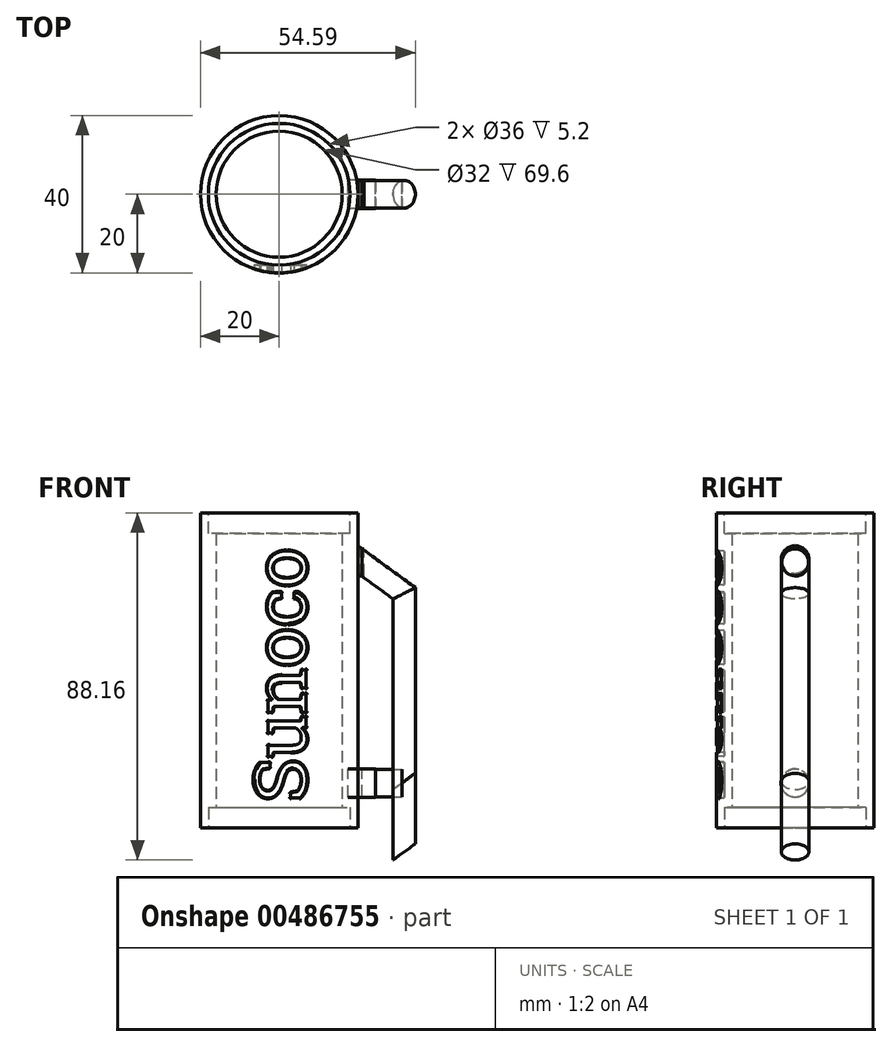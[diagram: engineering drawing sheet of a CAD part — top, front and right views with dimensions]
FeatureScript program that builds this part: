
annotation { "Feature Type Name" : "Feature", "Feature Type Description" : "" }
export const myFeature = defineFeature(function(context is Context, id is Id, definition is map)
    precondition{}
    {
        {
            var Q0;
            Q0=qCreatedBy(makeId("Top.planeOp"),FACE);
            var sketch = newSketch(context, id + "F0", { "sketchPlane" : qUnion([Q0])});
            skCircle(sketch, "E0", {"center": v(0, 0) * mm, "radius": 20 * mm});
            skSolve(sketch);
        }
        {
            var Q0;
            Q0 = qSketchRegion(id + "F0", true);
            extrude(context, id + "F1", {"entities" : qUnion([Q0]), "depth" : 80 * mm, "offsetDistance" : 25 * mm});
        }
        {
            var Q0;
            Q0=makeQuery(id+"F1.opExtrude","CAP_FACE",FACE,{"disambiguationData":[OSD([sQuery(id+"F0.wireOp",EDGE,"E0")])],"isStart":false});
            shell(context, id + "F2", {"entities" : qUnion([Q0]), "thickness" : 4 * mm});
        }
        {
            var Q0;
            Q0=makeQuery(id+"F1.opExtrude","CAP_FACE",FACE,{"disambiguationData":[OSD([sQuery(id+"F0.wireOp",EDGE,"E0")])],"isStart":false});
            var sketch = newSketch(context, id + "F3", { "sketchPlane" : qUnion([Q0])});
            skCircle(sketch, "E1.0", {"center": v(0, 0) * mm, "radius": 16 * mm});
            skCircle(sketch, "E2", {"center": v(0, 0) * mm, "radius": 18 * mm});
            skSolve(sketch);
        }
        {
            var Q0;
            Q0 = qSketchRegion(id + "F3", true);
            extrude(context, id + "F4", {"entities" : qUnion([Q0]), "operationType" : NewBodyOperationType.REMOVE, "oppositeDirection" : true, "depth" : 5.2 * mm, "offsetDistance" : 25 * mm});
        }
        {
            var Q0;
            Q0=makeQuery(id+"F1.opExtrude","CAP_FACE",FACE,{"disambiguationData":[OSD([sQuery(id+"F0.wireOp",EDGE,"E0")])],"isStart":false});
            var sketch = newSketch(context, id + "F5", { "sketchPlane" : qUnion([Q0])});
            skCircle(sketch, "E3.0", {"center": v(0, 0) * mm, "radius": 20 * mm});
            skCircle(sketch, "E4", {"center": v(-18.47, 7.67) * mm, "radius": 1 * mm});
            skSolve(sketch);
        }
        {
            var Q0;
            Q0=qCreatedBy(makeId("Front.planeOp"),FACE);
            cPlane(context, id + "F6", {"entities" : qUnion([Q0]), "cplaneType" : CPlaneType.OFFSET, "offset" : 20 * mm, "width" : 150 * mm, "height" : 150 * mm});
        }
        {
            var Q0;
            Q0=qCreatedBy(id+"F6.planeOp",FACE);
            var sketch = newSketch(context, id + "F7", { "sketchPlane" : qUnion([Q0])});
            skText(sketch, "E5", { "text": "Sunoco", "fontName": "RobotoSlab-Regular.ttf"});
            const initialGuessF7  = {"E5": [0.00686, 0.0065, 0, 1, 0.01323]};
            skSetInitialGuess(sketch, initialGuessF7);
            skSolve(sketch);
        }
        {
            var Q0;
            Q0 = qSketchRegion(id + "F7", true);
            extrude(context, id + "F8", {"entities" : qUnion([Q0]), "operationType" : NewBodyOperationType.REMOVE, "oppositeDirection" : true, "depth" : 1.5 * mm, "offsetDistance" : 25 * mm});
        }
        {
            var Q0;
            Q0 = qSketchRegion(id + "F7", true);
            extrude(context, id + "F9", {"entities" : qUnion([Q0]), "operationType" : NewBodyOperationType.REMOVE, "oppositeDirection" : true, "depth" : 2 * mm, "offsetDistance" : 25 * mm});
        }
        {
            var Q0;
            {var subQ0=sQuery(id+"F7.wireOp",EDGE,"E5.sketch_text.stroke-26");Q0=makeQuery(id+"F9.boolean.opBoolean","MERGE",FACE,{"derivedFrom":[makeQuery(id+"F8.boolean.opBoolean","COPY",FACE,{"derivedFrom":makeQuery(id+"F8.opExtrude","SWEPT_FACE",FACE,{"disambiguationData":[OSD([subQ0])]})}),makeQuery(id+"F9.opExtrude","SWEPT_FACE",FACE,{"disambiguationData":[OSD([subQ0])]})]});}
            var Q1;
            {var subQ0=sQuery(id+"F7.wireOp",EDGE,"E5.sketch_text.stroke-27");Q1=makeQuery(id+"F9.boolean.opBoolean","MERGE",FACE,{"derivedFrom":[makeQuery(id+"F8.boolean.opBoolean","COPY",FACE,{"derivedFrom":makeQuery(id+"F8.opExtrude","SWEPT_FACE",FACE,{"disambiguationData":[OSD([subQ0])]})}),makeQuery(id+"F9.opExtrude","SWEPT_FACE",FACE,{"disambiguationData":[OSD([subQ0])]})]});}
            var Q2;
            {var subQ0=sQuery(id+"F7.wireOp",EDGE,"E5.sketch_text.stroke-24");Q2=makeQuery(id+"F9.boolean.opBoolean","MERGE",FACE,{"derivedFrom":[makeQuery(id+"F8.boolean.opBoolean","COPY",FACE,{"derivedFrom":makeQuery(id+"F8.opExtrude","SWEPT_FACE",FACE,{"disambiguationData":[OSD([subQ0])]})}),makeQuery(id+"F9.opExtrude","SWEPT_FACE",FACE,{"disambiguationData":[OSD([subQ0])]})]});}
            var Q3;
            {var subQ0=sQuery(id+"F7.wireOp",EDGE,"E5.sketch_text.stroke-23");Q3=makeQuery(id+"F9.boolean.opBoolean","MERGE",FACE,{"derivedFrom":[makeQuery(id+"F8.boolean.opBoolean","COPY",FACE,{"derivedFrom":makeQuery(id+"F8.opExtrude","SWEPT_FACE",FACE,{"disambiguationData":[OSD([subQ0])]})}),makeQuery(id+"F9.opExtrude","SWEPT_FACE",FACE,{"disambiguationData":[OSD([subQ0])]})]});}
            var Q4;
            {var subQ0=sQuery(id+"F7.wireOp",EDGE,"E5.sketch_text.stroke-22");Q4=makeQuery(id+"F9.boolean.opBoolean","MERGE",FACE,{"derivedFrom":[makeQuery(id+"F8.boolean.opBoolean","COPY",FACE,{"derivedFrom":makeQuery(id+"F8.opExtrude","SWEPT_FACE",FACE,{"disambiguationData":[OSD([subQ0])]})}),makeQuery(id+"F9.opExtrude","SWEPT_FACE",FACE,{"disambiguationData":[OSD([subQ0])]})]});}
            var Q5;
            {var subQ0=sQuery(id+"F7.wireOp",EDGE,"E5.sketch_text.stroke-21");Q5=makeQuery(id+"F9.boolean.opBoolean","MERGE",FACE,{"derivedFrom":[makeQuery(id+"F8.boolean.opBoolean","COPY",FACE,{"derivedFrom":makeQuery(id+"F8.opExtrude","SWEPT_FACE",FACE,{"disambiguationData":[OSD([subQ0])]})}),makeQuery(id+"F9.opExtrude","SWEPT_FACE",FACE,{"disambiguationData":[OSD([subQ0])]})]});}
            var Q6;
            {var subQ0=sQuery(id+"F7.wireOp",EDGE,"E5.sketch_text.stroke-20");Q6=makeQuery(id+"F9.boolean.opBoolean","MERGE",FACE,{"derivedFrom":[makeQuery(id+"F8.boolean.opBoolean","COPY",FACE,{"derivedFrom":makeQuery(id+"F8.opExtrude","SWEPT_FACE",FACE,{"disambiguationData":[OSD([subQ0])]})}),makeQuery(id+"F9.opExtrude","SWEPT_FACE",FACE,{"disambiguationData":[OSD([subQ0])]})]});}
            var Q7;
            {var subQ0=sQuery(id+"F7.wireOp",EDGE,"E5.sketch_text.stroke-19");Q7=makeQuery(id+"F9.boolean.opBoolean","MERGE",FACE,{"derivedFrom":[makeQuery(id+"F8.boolean.opBoolean","COPY",FACE,{"derivedFrom":makeQuery(id+"F8.opExtrude","SWEPT_FACE",FACE,{"disambiguationData":[OSD([subQ0])]})}),makeQuery(id+"F9.opExtrude","SWEPT_FACE",FACE,{"disambiguationData":[OSD([subQ0])]})]});}
            var Q8;
            {var subQ0=sQuery(id+"F7.wireOp",EDGE,"E5.sketch_text.stroke-18");Q8=makeQuery(id+"F9.boolean.opBoolean","MERGE",FACE,{"derivedFrom":[makeQuery(id+"F8.boolean.opBoolean","COPY",FACE,{"derivedFrom":makeQuery(id+"F8.opExtrude","SWEPT_FACE",FACE,{"disambiguationData":[OSD([subQ0])]})}),makeQuery(id+"F9.opExtrude","SWEPT_FACE",FACE,{"disambiguationData":[OSD([subQ0])]})]});}
            var Q9;
            {var subQ0=sQuery(id+"F7.wireOp",EDGE,"E5.sketch_text.stroke-17");Q9=makeQuery(id+"F9.boolean.opBoolean","MERGE",FACE,{"derivedFrom":[makeQuery(id+"F8.boolean.opBoolean","COPY",FACE,{"derivedFrom":makeQuery(id+"F8.opExtrude","SWEPT_FACE",FACE,{"disambiguationData":[OSD([subQ0])]})}),makeQuery(id+"F9.opExtrude","SWEPT_FACE",FACE,{"disambiguationData":[OSD([subQ0])]})]});}
            var Q10;
            {var subQ0=sQuery(id+"F7.wireOp",EDGE,"E5.sketch_text.stroke-16");Q10=makeQuery(id+"F9.boolean.opBoolean","MERGE",FACE,{"derivedFrom":[makeQuery(id+"F8.boolean.opBoolean","COPY",FACE,{"derivedFrom":makeQuery(id+"F8.opExtrude","SWEPT_FACE",FACE,{"disambiguationData":[OSD([subQ0])]})}),makeQuery(id+"F9.opExtrude","SWEPT_FACE",FACE,{"disambiguationData":[OSD([subQ0])]})]});}
            var Q11;
            {var subQ0=sQuery(id+"F7.wireOp",EDGE,"E5.sketch_text.stroke-15");Q11=makeQuery(id+"F9.boolean.opBoolean","MERGE",FACE,{"derivedFrom":[makeQuery(id+"F8.boolean.opBoolean","COPY",FACE,{"derivedFrom":makeQuery(id+"F8.opExtrude","SWEPT_FACE",FACE,{"disambiguationData":[OSD([subQ0])]})}),makeQuery(id+"F9.opExtrude","SWEPT_FACE",FACE,{"disambiguationData":[OSD([subQ0])]})]});}
            var Q12;
            {var subQ0=sQuery(id+"F7.wireOp",EDGE,"E5.sketch_text.stroke-14");Q12=makeQuery(id+"F9.boolean.opBoolean","MERGE",FACE,{"derivedFrom":[makeQuery(id+"F8.boolean.opBoolean","COPY",FACE,{"derivedFrom":makeQuery(id+"F8.opExtrude","SWEPT_FACE",FACE,{"disambiguationData":[OSD([subQ0])]})}),makeQuery(id+"F9.opExtrude","SWEPT_FACE",FACE,{"disambiguationData":[OSD([subQ0])]})]});}
            var Q13;
            {var subQ0=sQuery(id+"F7.wireOp",EDGE,"E5.sketch_text.stroke-13");Q13=makeQuery(id+"F9.boolean.opBoolean","MERGE",FACE,{"derivedFrom":[makeQuery(id+"F8.boolean.opBoolean","COPY",FACE,{"derivedFrom":makeQuery(id+"F8.opExtrude","SWEPT_FACE",FACE,{"disambiguationData":[OSD([subQ0])]})}),makeQuery(id+"F9.opExtrude","SWEPT_FACE",FACE,{"disambiguationData":[OSD([subQ0])]})]});}
            var Q14;
            {var subQ0=sQuery(id+"F7.wireOp",EDGE,"E5.sketch_text.stroke-12");Q14=makeQuery(id+"F9.boolean.opBoolean","MERGE",FACE,{"derivedFrom":[makeQuery(id+"F8.boolean.opBoolean","COPY",FACE,{"derivedFrom":makeQuery(id+"F8.opExtrude","SWEPT_FACE",FACE,{"disambiguationData":[OSD([subQ0])]})}),makeQuery(id+"F9.opExtrude","SWEPT_FACE",FACE,{"disambiguationData":[OSD([subQ0])]})]});}
            var Q15;
            {var subQ0=sQuery(id+"F7.wireOp",EDGE,"E5.sketch_text.stroke-11");Q15=makeQuery(id+"F9.boolean.opBoolean","MERGE",FACE,{"derivedFrom":[makeQuery(id+"F8.boolean.opBoolean","COPY",FACE,{"derivedFrom":makeQuery(id+"F8.opExtrude","SWEPT_FACE",FACE,{"disambiguationData":[OSD([subQ0])]})}),makeQuery(id+"F9.opExtrude","SWEPT_FACE",FACE,{"disambiguationData":[OSD([subQ0])]})]});}
            var Q16;
            {var subQ0=sQuery(id+"F7.wireOp",EDGE,"E5.sketch_text.stroke-10");Q16=makeQuery(id+"F9.boolean.opBoolean","MERGE",FACE,{"derivedFrom":[makeQuery(id+"F8.boolean.opBoolean","COPY",FACE,{"derivedFrom":makeQuery(id+"F8.opExtrude","SWEPT_FACE",FACE,{"disambiguationData":[OSD([subQ0])]})}),makeQuery(id+"F9.opExtrude","SWEPT_FACE",FACE,{"disambiguationData":[OSD([subQ0])]})]});}
            var Q17;
            {var subQ0=sQuery(id+"F7.wireOp",EDGE,"E5.sketch_text.stroke-9");Q17=makeQuery(id+"F9.boolean.opBoolean","MERGE",FACE,{"derivedFrom":[makeQuery(id+"F8.boolean.opBoolean","COPY",FACE,{"derivedFrom":makeQuery(id+"F8.opExtrude","SWEPT_FACE",FACE,{"disambiguationData":[OSD([subQ0])]})}),makeQuery(id+"F9.opExtrude","SWEPT_FACE",FACE,{"disambiguationData":[OSD([subQ0])]})]});}
            var Q18;
            {var subQ0=sQuery(id+"F7.wireOp",EDGE,"E5.sketch_text.stroke-8");Q18=makeQuery(id+"F9.boolean.opBoolean","MERGE",FACE,{"derivedFrom":[makeQuery(id+"F8.boolean.opBoolean","COPY",FACE,{"derivedFrom":makeQuery(id+"F8.opExtrude","SWEPT_FACE",FACE,{"disambiguationData":[OSD([subQ0])]})}),makeQuery(id+"F9.opExtrude","SWEPT_FACE",FACE,{"disambiguationData":[OSD([subQ0])]})]});}
            var Q19;
            {var subQ0=sQuery(id+"F7.wireOp",EDGE,"E5.sketch_text.stroke-7");Q19=makeQuery(id+"F9.boolean.opBoolean","MERGE",FACE,{"derivedFrom":[makeQuery(id+"F8.boolean.opBoolean","COPY",FACE,{"derivedFrom":makeQuery(id+"F8.opExtrude","SWEPT_FACE",FACE,{"disambiguationData":[OSD([subQ0])]})}),makeQuery(id+"F9.opExtrude","SWEPT_FACE",FACE,{"disambiguationData":[OSD([subQ0])]})]});}
            var Q20;
            {var subQ0=sQuery(id+"F7.wireOp",EDGE,"E5.sketch_text.stroke-6");Q20=makeQuery(id+"F9.boolean.opBoolean","MERGE",FACE,{"derivedFrom":[makeQuery(id+"F8.boolean.opBoolean","COPY",FACE,{"derivedFrom":makeQuery(id+"F8.opExtrude","SWEPT_FACE",FACE,{"disambiguationData":[OSD([subQ0])]})}),makeQuery(id+"F9.opExtrude","SWEPT_FACE",FACE,{"disambiguationData":[OSD([subQ0])]})]});}
            var Q21;
            {var subQ0=sQuery(id+"F7.wireOp",EDGE,"E5.sketch_text.stroke-5");Q21=makeQuery(id+"F9.boolean.opBoolean","MERGE",FACE,{"derivedFrom":[makeQuery(id+"F8.boolean.opBoolean","COPY",FACE,{"derivedFrom":makeQuery(id+"F8.opExtrude","SWEPT_FACE",FACE,{"disambiguationData":[OSD([subQ0])]})}),makeQuery(id+"F9.opExtrude","SWEPT_FACE",FACE,{"disambiguationData":[OSD([subQ0])]})]});}
            var Q22;
            {var subQ0=sQuery(id+"F7.wireOp",EDGE,"E5.sketch_text.stroke-4");Q22=makeQuery(id+"F9.boolean.opBoolean","MERGE",FACE,{"derivedFrom":[makeQuery(id+"F8.boolean.opBoolean","COPY",FACE,{"derivedFrom":makeQuery(id+"F8.opExtrude","SWEPT_FACE",FACE,{"disambiguationData":[OSD([subQ0])]})}),makeQuery(id+"F9.opExtrude","SWEPT_FACE",FACE,{"disambiguationData":[OSD([subQ0])]})]});}
            var Q23;
            {var subQ0=sQuery(id+"F7.wireOp",EDGE,"E5.sketch_text.stroke-3");Q23=makeQuery(id+"F9.boolean.opBoolean","MERGE",FACE,{"derivedFrom":[makeQuery(id+"F8.boolean.opBoolean","COPY",FACE,{"derivedFrom":makeQuery(id+"F8.opExtrude","SWEPT_FACE",FACE,{"disambiguationData":[OSD([subQ0])]})}),makeQuery(id+"F9.opExtrude","SWEPT_FACE",FACE,{"disambiguationData":[OSD([subQ0])]})]});}
            var Q24;
            Q24=makeQuery(id+"F8.boolean.opBoolean","INTERSECT",EDGE,{"derivedFrom":[makeQuery(id+"F1.opExtrude","SWEPT_FACE",FACE,{"disambiguationData":[OSD([sQuery(id+"F0.wireOp",EDGE,"E0")])]}),makeQuery(id+"F8.opExtrude","SWEPT_FACE",FACE,{"disambiguationData":[OSD([sQuery(id+"F7.wireOp",EDGE,"E5.sketch_text.stroke-2")])]})]});
            var Q25;
            Q25=makeQuery(id+"F9.boolean.opBoolean","COPY",EDGE,{"derivedFrom":makeQuery(id+"F9.opExtrude","CAP_EDGE",EDGE,{"disambiguationData":[OSD([sQuery(id+"F7.wireOp",EDGE,"E5.sketch_text.stroke-2")])],"isStart":false})});
            var Q26;
            {var subQ0=sQuery(id+"F7.wireOp",EDGE,"E5.sketch_text.stroke-2");Q26=makeQuery(id+"F9.boolean.opBoolean","MERGE",FACE,{"derivedFrom":[makeQuery(id+"F8.boolean.opBoolean","COPY",FACE,{"derivedFrom":makeQuery(id+"F8.opExtrude","SWEPT_FACE",FACE,{"disambiguationData":[OSD([subQ0])]})}),makeQuery(id+"F9.opExtrude","SWEPT_FACE",FACE,{"disambiguationData":[OSD([subQ0])]})]});}
            var Q27;
            {var subQ0=sQuery(id+"F7.wireOp",EDGE,"E5.sketch_text.stroke-1");Q27=makeQuery(id+"F9.boolean.opBoolean","MERGE",FACE,{"derivedFrom":[makeQuery(id+"F8.boolean.opBoolean","COPY",FACE,{"derivedFrom":makeQuery(id+"F8.opExtrude","SWEPT_FACE",FACE,{"disambiguationData":[OSD([subQ0])]})}),makeQuery(id+"F9.opExtrude","SWEPT_FACE",FACE,{"disambiguationData":[OSD([subQ0])]})]});}
            var Q28;
            {var subQ0=sQuery(id+"F7.wireOp",EDGE,"E5.sketch_text.stroke-0");Q28=makeQuery(id+"F9.boolean.opBoolean","MERGE",FACE,{"derivedFrom":[makeQuery(id+"F8.boolean.opBoolean","COPY",FACE,{"derivedFrom":makeQuery(id+"F8.opExtrude","SWEPT_FACE",FACE,{"disambiguationData":[OSD([subQ0])]})}),makeQuery(id+"F9.opExtrude","SWEPT_FACE",FACE,{"disambiguationData":[OSD([subQ0])]})]});}
            fillet(context, id + "F10", {"entities" : qUnion([Q0, Q1, Q2, Q3, Q4, Q5, Q6, Q7, Q8, Q9, Q10, Q11, Q12, Q13, Q14, Q15, Q16, Q17, Q18, Q19, Q20, Q21, Q22, Q23, Q24, Q25, Q26, Q27, Q28]), "radius" : .2 * mm, "tangentPropagation" : true, "allowEdgeOverflow" : false});
        }
        {
            var Q0;
            {var subQ0=sQuery(id+"F7.wireOp",EDGE,"E5.sketch_text.stroke-38");var subQ1=sQuery(id+"F7.wireOp",EDGE,"E5.sketch_text.stroke-37");Q0=makeQuery(id+"F9.boolean.opBoolean","MERGE",FACE,{"derivedFrom":[makeQuery(id+"F8.boolean.opBoolean","COPY",FACE,{"derivedFrom":makeQuery(id+"F8.opExtrude","SWEPT_FACE",FACE,{"disambiguationData":[OSD([subQ1,subQ0])]})}),makeQuery(id+"F9.opExtrude","SWEPT_FACE",FACE,{"disambiguationData":[OSD([subQ1,subQ0])]})]});}
            var Q1;
            {var subQ0=sQuery(id+"F7.wireOp",EDGE,"E5.sketch_text.stroke-36");Q1=makeQuery(id+"F9.boolean.opBoolean","MERGE",FACE,{"derivedFrom":[makeQuery(id+"F8.boolean.opBoolean","COPY",FACE,{"derivedFrom":makeQuery(id+"F8.opExtrude","SWEPT_FACE",FACE,{"disambiguationData":[OSD([subQ0])]})}),makeQuery(id+"F9.opExtrude","SWEPT_FACE",FACE,{"disambiguationData":[OSD([subQ0])]})]});}
            var Q2;
            {var subQ0=sQuery(id+"F7.wireOp",EDGE,"E5.sketch_text.stroke-35");Q2=makeQuery(id+"F9.boolean.opBoolean","MERGE",FACE,{"derivedFrom":[makeQuery(id+"F8.boolean.opBoolean","COPY",FACE,{"derivedFrom":makeQuery(id+"F8.opExtrude","SWEPT_FACE",FACE,{"disambiguationData":[OSD([subQ0])]})}),makeQuery(id+"F9.opExtrude","SWEPT_FACE",FACE,{"disambiguationData":[OSD([subQ0])]})]});}
            var Q3;
            {var subQ0=sQuery(id+"F7.wireOp",EDGE,"E5.sketch_text.stroke-34");Q3=makeQuery(id+"F9.boolean.opBoolean","MERGE",FACE,{"derivedFrom":[makeQuery(id+"F8.boolean.opBoolean","COPY",FACE,{"derivedFrom":makeQuery(id+"F8.opExtrude","SWEPT_FACE",FACE,{"disambiguationData":[OSD([subQ0])]})}),makeQuery(id+"F9.opExtrude","SWEPT_FACE",FACE,{"disambiguationData":[OSD([subQ0])]})]});}
            var Q4;
            {var subQ0=sQuery(id+"F7.wireOp",EDGE,"E5.sketch_text.stroke-44");Q4=makeQuery(id+"F9.boolean.opBoolean","MERGE",FACE,{"derivedFrom":[makeQuery(id+"F8.boolean.opBoolean","COPY",FACE,{"derivedFrom":makeQuery(id+"F8.opExtrude","SWEPT_FACE",FACE,{"disambiguationData":[OSD([subQ0])]})}),makeQuery(id+"F9.opExtrude","SWEPT_FACE",FACE,{"disambiguationData":[OSD([subQ0])]})]});}
            var Q5;
            {var subQ0=sQuery(id+"F7.wireOp",EDGE,"E5.sketch_text.stroke-45");Q5=makeQuery(id+"F9.boolean.opBoolean","MERGE",FACE,{"derivedFrom":[makeQuery(id+"F8.boolean.opBoolean","COPY",FACE,{"derivedFrom":makeQuery(id+"F8.opExtrude","SWEPT_FACE",FACE,{"disambiguationData":[OSD([subQ0])]})}),makeQuery(id+"F9.opExtrude","SWEPT_FACE",FACE,{"disambiguationData":[OSD([subQ0])]})]});}
            var Q6;
            {var subQ0=sQuery(id+"F7.wireOp",EDGE,"E5.sketch_text.stroke-46");Q6=makeQuery(id+"F9.boolean.opBoolean","MERGE",FACE,{"derivedFrom":[makeQuery(id+"F8.boolean.opBoolean","COPY",FACE,{"derivedFrom":makeQuery(id+"F8.opExtrude","SWEPT_FACE",FACE,{"disambiguationData":[OSD([subQ0])]})}),makeQuery(id+"F9.opExtrude","SWEPT_FACE",FACE,{"disambiguationData":[OSD([subQ0])]})]});}
            var Q7;
            {var subQ0=sQuery(id+"F7.wireOp",EDGE,"E5.sketch_text.stroke-48");var subQ1=sQuery(id+"F7.wireOp",EDGE,"E5.sketch_text.stroke-47");Q7=makeQuery(id+"F9.boolean.opBoolean","MERGE",FACE,{"derivedFrom":[makeQuery(id+"F8.boolean.opBoolean","COPY",FACE,{"derivedFrom":makeQuery(id+"F8.opExtrude","SWEPT_FACE",FACE,{"disambiguationData":[OSD([subQ1,subQ0])]})}),makeQuery(id+"F9.opExtrude","SWEPT_FACE",FACE,{"disambiguationData":[OSD([subQ1,subQ0])]})]});}
            var Q8;
            {var subQ0=sQuery(id+"F7.wireOp",EDGE,"E5.sketch_text.stroke-49");Q8=makeQuery(id+"F9.boolean.opBoolean","MERGE",FACE,{"derivedFrom":[makeQuery(id+"F8.boolean.opBoolean","COPY",FACE,{"derivedFrom":makeQuery(id+"F8.opExtrude","SWEPT_FACE",FACE,{"disambiguationData":[OSD([subQ0])]})}),makeQuery(id+"F9.opExtrude","SWEPT_FACE",FACE,{"disambiguationData":[OSD([subQ0])]})]});}
            var Q9;
            {var subQ0=sQuery(id+"F7.wireOp",EDGE,"E5.sketch_text.stroke-52");Q9=makeQuery(id+"F9.boolean.opBoolean","MERGE",FACE,{"derivedFrom":[makeQuery(id+"F8.boolean.opBoolean","COPY",FACE,{"derivedFrom":makeQuery(id+"F8.opExtrude","SWEPT_FACE",FACE,{"disambiguationData":[OSD([subQ0])]})}),makeQuery(id+"F9.opExtrude","SWEPT_FACE",FACE,{"disambiguationData":[OSD([subQ0])]})]});}
            var Q10;
            {var subQ0=sQuery(id+"F7.wireOp",EDGE,"E5.sketch_text.stroke-53");Q10=makeQuery(id+"F9.boolean.opBoolean","MERGE",FACE,{"derivedFrom":[makeQuery(id+"F8.boolean.opBoolean","COPY",FACE,{"derivedFrom":makeQuery(id+"F8.opExtrude","SWEPT_FACE",FACE,{"disambiguationData":[OSD([subQ0])]})}),makeQuery(id+"F9.opExtrude","SWEPT_FACE",FACE,{"disambiguationData":[OSD([subQ0])]})]});}
            var Q11;
            {var subQ0=sQuery(id+"F7.wireOp",EDGE,"E5.sketch_text.stroke-50");Q11=makeQuery(id+"F9.boolean.opBoolean","MERGE",FACE,{"derivedFrom":[makeQuery(id+"F8.boolean.opBoolean","COPY",FACE,{"derivedFrom":makeQuery(id+"F8.opExtrude","SWEPT_FACE",FACE,{"disambiguationData":[OSD([subQ0])]})}),makeQuery(id+"F9.opExtrude","SWEPT_FACE",FACE,{"disambiguationData":[OSD([subQ0])]})]});}
            var Q12;
            {var subQ0=sQuery(id+"F7.wireOp",EDGE,"E5.sketch_text.stroke-78");Q12=makeQuery(id+"F9.boolean.opBoolean","MERGE",FACE,{"derivedFrom":[makeQuery(id+"F8.boolean.opBoolean","COPY",FACE,{"derivedFrom":makeQuery(id+"F8.opExtrude","SWEPT_FACE",FACE,{"disambiguationData":[OSD([subQ0])]})}),makeQuery(id+"F9.opExtrude","SWEPT_FACE",FACE,{"disambiguationData":[OSD([subQ0])]})]});}
            var Q13;
            {var subQ0=sQuery(id+"F7.wireOp",EDGE,"E5.sketch_text.stroke-79");Q13=makeQuery(id+"F9.boolean.opBoolean","MERGE",FACE,{"derivedFrom":[makeQuery(id+"F8.boolean.opBoolean","COPY",FACE,{"derivedFrom":makeQuery(id+"F8.opExtrude","SWEPT_FACE",FACE,{"disambiguationData":[OSD([subQ0])]})}),makeQuery(id+"F9.opExtrude","SWEPT_FACE",FACE,{"disambiguationData":[OSD([subQ0])]})]});}
            var Q14;
            {var subQ0=sQuery(id+"F7.wireOp",EDGE,"E5.sketch_text.stroke-54");Q14=makeQuery(id+"F9.boolean.opBoolean","MERGE",FACE,{"derivedFrom":[makeQuery(id+"F8.boolean.opBoolean","COPY",FACE,{"derivedFrom":makeQuery(id+"F8.opExtrude","SWEPT_FACE",FACE,{"disambiguationData":[OSD([subQ0])]})}),makeQuery(id+"F9.opExtrude","SWEPT_FACE",FACE,{"disambiguationData":[OSD([subQ0])]})]});}
            var Q15;
            {var subQ0=sQuery(id+"F7.wireOp",EDGE,"E5.sketch_text.stroke-55");Q15=makeQuery(id+"F9.boolean.opBoolean","MERGE",FACE,{"derivedFrom":[makeQuery(id+"F8.boolean.opBoolean","COPY",FACE,{"derivedFrom":makeQuery(id+"F8.opExtrude","SWEPT_FACE",FACE,{"disambiguationData":[OSD([subQ0])]})}),makeQuery(id+"F9.opExtrude","SWEPT_FACE",FACE,{"disambiguationData":[OSD([subQ0])]})]});}
            var Q16;
            {var subQ0=sQuery(id+"F7.wireOp",EDGE,"E5.sketch_text.stroke-56");Q16=makeQuery(id+"F9.boolean.opBoolean","MERGE",FACE,{"derivedFrom":[makeQuery(id+"F8.boolean.opBoolean","COPY",FACE,{"derivedFrom":makeQuery(id+"F8.opExtrude","SWEPT_FACE",FACE,{"disambiguationData":[OSD([subQ0])]})}),makeQuery(id+"F9.opExtrude","SWEPT_FACE",FACE,{"disambiguationData":[OSD([subQ0])]})]});}
            var Q17;
            {var subQ0=sQuery(id+"F7.wireOp",EDGE,"E5.sketch_text.stroke-57");Q17=makeQuery(id+"F9.boolean.opBoolean","MERGE",FACE,{"derivedFrom":[makeQuery(id+"F8.boolean.opBoolean","COPY",FACE,{"derivedFrom":makeQuery(id+"F8.opExtrude","SWEPT_FACE",FACE,{"disambiguationData":[OSD([subQ0])]})}),makeQuery(id+"F9.opExtrude","SWEPT_FACE",FACE,{"disambiguationData":[OSD([subQ0])]})]});}
            var Q18;
            {var subQ0=sQuery(id+"F7.wireOp",EDGE,"E5.sketch_text.stroke-58");Q18=makeQuery(id+"F9.boolean.opBoolean","MERGE",FACE,{"derivedFrom":[makeQuery(id+"F8.boolean.opBoolean","COPY",FACE,{"derivedFrom":makeQuery(id+"F8.opExtrude","SWEPT_FACE",FACE,{"disambiguationData":[OSD([subQ0])]})}),makeQuery(id+"F9.opExtrude","SWEPT_FACE",FACE,{"disambiguationData":[OSD([subQ0])]})]});}
            var Q19;
            {var subQ0=sQuery(id+"F7.wireOp",EDGE,"E5.sketch_text.stroke-59");Q19=makeQuery(id+"F9.boolean.opBoolean","MERGE",FACE,{"derivedFrom":[makeQuery(id+"F8.boolean.opBoolean","COPY",FACE,{"derivedFrom":makeQuery(id+"F8.opExtrude","SWEPT_FACE",FACE,{"disambiguationData":[OSD([subQ0])]})}),makeQuery(id+"F9.opExtrude","SWEPT_FACE",FACE,{"disambiguationData":[OSD([subQ0])]})]});}
            var Q20;
            {var subQ0=sQuery(id+"F7.wireOp",EDGE,"E5.sketch_text.stroke-75");Q20=makeQuery(id+"F9.boolean.opBoolean","MERGE",FACE,{"derivedFrom":[makeQuery(id+"F8.boolean.opBoolean","COPY",FACE,{"derivedFrom":makeQuery(id+"F8.opExtrude","SWEPT_FACE",FACE,{"disambiguationData":[OSD([subQ0])]})}),makeQuery(id+"F9.opExtrude","SWEPT_FACE",FACE,{"disambiguationData":[OSD([subQ0])]})]});}
            var Q21;
            {var subQ0=sQuery(id+"F7.wireOp",EDGE,"E5.sketch_text.stroke-76");Q21=makeQuery(id+"F9.boolean.opBoolean","MERGE",FACE,{"derivedFrom":[makeQuery(id+"F8.boolean.opBoolean","COPY",FACE,{"derivedFrom":makeQuery(id+"F8.opExtrude","SWEPT_FACE",FACE,{"disambiguationData":[OSD([subQ0])]})}),makeQuery(id+"F9.opExtrude","SWEPT_FACE",FACE,{"disambiguationData":[OSD([subQ0])]})]});}
            var Q22;
            {var subQ0=sQuery(id+"F7.wireOp",EDGE,"E5.sketch_text.stroke-74");Q22=makeQuery(id+"F9.boolean.opBoolean","MERGE",FACE,{"derivedFrom":[makeQuery(id+"F8.boolean.opBoolean","COPY",FACE,{"derivedFrom":makeQuery(id+"F8.opExtrude","SWEPT_FACE",FACE,{"disambiguationData":[OSD([subQ0])]})}),makeQuery(id+"F9.opExtrude","SWEPT_FACE",FACE,{"disambiguationData":[OSD([subQ0])]})]});}
            var Q23;
            {var subQ0=sQuery(id+"F7.wireOp",EDGE,"E5.sketch_text.stroke-73");Q23=makeQuery(id+"F9.boolean.opBoolean","MERGE",FACE,{"derivedFrom":[makeQuery(id+"F8.boolean.opBoolean","COPY",FACE,{"derivedFrom":makeQuery(id+"F8.opExtrude","SWEPT_FACE",FACE,{"disambiguationData":[OSD([subQ0])]})}),makeQuery(id+"F9.opExtrude","SWEPT_FACE",FACE,{"disambiguationData":[OSD([subQ0])]})]});}
            var Q24;
            Q24=makeQuery(id+"F8.boolean.opBoolean","INTERSECT",EDGE,{"derivedFrom":[makeQuery(id+"F1.opExtrude","SWEPT_FACE",FACE,{"disambiguationData":[OSD([sQuery(id+"F0.wireOp",EDGE,"E0")])]}),makeQuery(id+"F8.opExtrude","SWEPT_FACE",FACE,{"disambiguationData":[OSD([sQuery(id+"F7.wireOp",EDGE,"E5.sketch_text.stroke-72")])]})]});
            var Q25;
            {var subQ0=sQuery(id+"F7.wireOp",EDGE,"E5.sketch_text.stroke-72");Q25=makeQuery(id+"F9.boolean.opBoolean","MERGE",FACE,{"derivedFrom":[makeQuery(id+"F8.boolean.opBoolean","COPY",FACE,{"derivedFrom":makeQuery(id+"F8.opExtrude","SWEPT_FACE",FACE,{"disambiguationData":[OSD([subQ0])]})}),makeQuery(id+"F9.opExtrude","SWEPT_FACE",FACE,{"disambiguationData":[OSD([subQ0])]})]});}
            var Q26;
            {var subQ0=sQuery(id+"F7.wireOp",EDGE,"E5.sketch_text.stroke-71");Q26=makeQuery(id+"F9.boolean.opBoolean","MERGE",FACE,{"derivedFrom":[makeQuery(id+"F8.boolean.opBoolean","COPY",FACE,{"derivedFrom":makeQuery(id+"F8.opExtrude","SWEPT_FACE",FACE,{"disambiguationData":[OSD([subQ0])]})}),makeQuery(id+"F9.opExtrude","SWEPT_FACE",FACE,{"disambiguationData":[OSD([subQ0])]})]});}
            var Q27;
            {var subQ0=sQuery(id+"F7.wireOp",EDGE,"E5.sketch_text.stroke-70");Q27=makeQuery(id+"F9.boolean.opBoolean","MERGE",FACE,{"derivedFrom":[makeQuery(id+"F8.boolean.opBoolean","COPY",FACE,{"derivedFrom":makeQuery(id+"F8.opExtrude","SWEPT_FACE",FACE,{"disambiguationData":[OSD([subQ0])]})}),makeQuery(id+"F9.opExtrude","SWEPT_FACE",FACE,{"disambiguationData":[OSD([subQ0])]})]});}
            var Q28;
            {var subQ0=sQuery(id+"F7.wireOp",EDGE,"E5.sketch_text.stroke-69");Q28=makeQuery(id+"F9.boolean.opBoolean","MERGE",FACE,{"derivedFrom":[makeQuery(id+"F8.boolean.opBoolean","COPY",FACE,{"derivedFrom":makeQuery(id+"F8.opExtrude","SWEPT_FACE",FACE,{"disambiguationData":[OSD([subQ0])]})}),makeQuery(id+"F9.opExtrude","SWEPT_FACE",FACE,{"disambiguationData":[OSD([subQ0])]})]});}
            var Q29;
            {var subQ0=sQuery(id+"F7.wireOp",EDGE,"E5.sketch_text.stroke-68");Q29=makeQuery(id+"F9.boolean.opBoolean","MERGE",FACE,{"derivedFrom":[makeQuery(id+"F8.boolean.opBoolean","COPY",FACE,{"derivedFrom":makeQuery(id+"F8.opExtrude","SWEPT_FACE",FACE,{"disambiguationData":[OSD([subQ0])]})}),makeQuery(id+"F9.opExtrude","SWEPT_FACE",FACE,{"disambiguationData":[OSD([subQ0])]})]});}
            var Q30;
            {var subQ0=sQuery(id+"F7.wireOp",EDGE,"E5.sketch_text.stroke-67");Q30=makeQuery(id+"F9.boolean.opBoolean","MERGE",FACE,{"derivedFrom":[makeQuery(id+"F8.boolean.opBoolean","COPY",FACE,{"derivedFrom":makeQuery(id+"F8.opExtrude","SWEPT_FACE",FACE,{"disambiguationData":[OSD([subQ0])]})}),makeQuery(id+"F9.opExtrude","SWEPT_FACE",FACE,{"disambiguationData":[OSD([subQ0])]})]});}
            var Q31;
            {var subQ0=sQuery(id+"F7.wireOp",EDGE,"E5.sketch_text.stroke-66");Q31=makeQuery(id+"F9.boolean.opBoolean","MERGE",FACE,{"derivedFrom":[makeQuery(id+"F8.boolean.opBoolean","COPY",FACE,{"derivedFrom":makeQuery(id+"F8.opExtrude","SWEPT_FACE",FACE,{"disambiguationData":[OSD([subQ0])]})}),makeQuery(id+"F9.opExtrude","SWEPT_FACE",FACE,{"disambiguationData":[OSD([subQ0])]})]});}
            var Q32;
            {var subQ0=sQuery(id+"F7.wireOp",EDGE,"E5.sketch_text.stroke-65");Q32=makeQuery(id+"F9.boolean.opBoolean","MERGE",FACE,{"derivedFrom":[makeQuery(id+"F8.boolean.opBoolean","COPY",FACE,{"derivedFrom":makeQuery(id+"F8.opExtrude","SWEPT_FACE",FACE,{"disambiguationData":[OSD([subQ0])]})}),makeQuery(id+"F9.opExtrude","SWEPT_FACE",FACE,{"disambiguationData":[OSD([subQ0])]})]});}
            var Q33;
            {var subQ0=sQuery(id+"F7.wireOp",EDGE,"E5.sketch_text.stroke-64");Q33=makeQuery(id+"F9.boolean.opBoolean","MERGE",FACE,{"derivedFrom":[makeQuery(id+"F8.boolean.opBoolean","COPY",FACE,{"derivedFrom":makeQuery(id+"F8.opExtrude","SWEPT_FACE",FACE,{"disambiguationData":[OSD([subQ0])]})}),makeQuery(id+"F9.opExtrude","SWEPT_FACE",FACE,{"disambiguationData":[OSD([subQ0])]})]});}
            var Q34;
            {var subQ0=sQuery(id+"F7.wireOp",EDGE,"E5.sketch_text.stroke-63");Q34=makeQuery(id+"F9.boolean.opBoolean","MERGE",FACE,{"derivedFrom":[makeQuery(id+"F8.boolean.opBoolean","COPY",FACE,{"derivedFrom":makeQuery(id+"F8.opExtrude","SWEPT_FACE",FACE,{"disambiguationData":[OSD([subQ0])]})}),makeQuery(id+"F9.opExtrude","SWEPT_FACE",FACE,{"disambiguationData":[OSD([subQ0])]})]});}
            var Q35;
            {var subQ0=sQuery(id+"F7.wireOp",EDGE,"E5.sketch_text.stroke-62");Q35=makeQuery(id+"F9.boolean.opBoolean","MERGE",FACE,{"derivedFrom":[makeQuery(id+"F8.boolean.opBoolean","COPY",FACE,{"derivedFrom":makeQuery(id+"F8.opExtrude","SWEPT_FACE",FACE,{"disambiguationData":[OSD([subQ0])]})}),makeQuery(id+"F9.opExtrude","SWEPT_FACE",FACE,{"disambiguationData":[OSD([subQ0])]})]});}
            var Q36;
            {var subQ0=sQuery(id+"F7.wireOp",EDGE,"E5.sketch_text.stroke-61");Q36=makeQuery(id+"F9.boolean.opBoolean","MERGE",FACE,{"derivedFrom":[makeQuery(id+"F8.boolean.opBoolean","COPY",FACE,{"derivedFrom":makeQuery(id+"F8.opExtrude","SWEPT_FACE",FACE,{"disambiguationData":[OSD([subQ0])]})}),makeQuery(id+"F9.opExtrude","SWEPT_FACE",FACE,{"disambiguationData":[OSD([subQ0])]})]});}
            var Q37;
            {var subQ0=sQuery(id+"F7.wireOp",EDGE,"E5.sketch_text.stroke-60");Q37=makeQuery(id+"F9.boolean.opBoolean","MERGE",FACE,{"derivedFrom":[makeQuery(id+"F8.boolean.opBoolean","COPY",FACE,{"derivedFrom":makeQuery(id+"F8.opExtrude","SWEPT_FACE",FACE,{"disambiguationData":[OSD([subQ0])]})}),makeQuery(id+"F9.opExtrude","SWEPT_FACE",FACE,{"disambiguationData":[OSD([subQ0])]})]});}
            fillet(context, id + "F11", {"entities" : qUnion([Q0, Q1, Q2, Q3, Q4, Q5, Q6, Q7, Q8, Q9, Q10, Q11, Q12, Q13, Q14, Q15, Q16, Q17, Q18, Q19, Q20, Q21, Q22, Q23, Q24, Q25, Q26, Q27, Q28, Q29, Q30, Q31, Q32, Q33, Q34, Q35, Q36, Q37]), "radius" : .2 * mm, "tangentPropagation" : true, "allowEdgeOverflow" : false});
        }
        {
            var Q0;
            {var subQ0=sQuery(id+"F7.wireOp",EDGE,"E5.sketch_text.stroke-85");Q0=makeQuery(id+"F9.boolean.opBoolean","MERGE",FACE,{"derivedFrom":[makeQuery(id+"F8.boolean.opBoolean","COPY",FACE,{"derivedFrom":makeQuery(id+"F8.opExtrude","SWEPT_FACE",FACE,{"disambiguationData":[OSD([subQ0])]})}),makeQuery(id+"F9.opExtrude","SWEPT_FACE",FACE,{"disambiguationData":[OSD([subQ0])]})]});}
            var Q1;
            {var subQ0=sQuery(id+"F7.wireOp",EDGE,"E5.sketch_text.stroke-95");Q1=makeQuery(id+"F9.boolean.opBoolean","MERGE",FACE,{"derivedFrom":[makeQuery(id+"F8.boolean.opBoolean","COPY",FACE,{"derivedFrom":makeQuery(id+"F8.opExtrude","SWEPT_FACE",FACE,{"disambiguationData":[OSD([subQ0])]})}),makeQuery(id+"F9.opExtrude","SWEPT_FACE",FACE,{"disambiguationData":[OSD([subQ0])]})]});}
            var Q2;
            {var subQ0=sQuery(id+"F7.wireOp",EDGE,"E5.sketch_text.stroke-96");Q2=makeQuery(id+"F9.boolean.opBoolean","MERGE",FACE,{"derivedFrom":[makeQuery(id+"F8.boolean.opBoolean","COPY",FACE,{"derivedFrom":makeQuery(id+"F8.opExtrude","SWEPT_FACE",FACE,{"disambiguationData":[OSD([subQ0])]})}),makeQuery(id+"F9.opExtrude","SWEPT_FACE",FACE,{"disambiguationData":[OSD([subQ0])]})]});}
            var Q3;
            {var subQ0=sQuery(id+"F7.wireOp",EDGE,"E5.sketch_text.stroke-97");Q3=makeQuery(id+"F9.boolean.opBoolean","MERGE",FACE,{"derivedFrom":[makeQuery(id+"F8.boolean.opBoolean","COPY",FACE,{"derivedFrom":makeQuery(id+"F8.opExtrude","SWEPT_FACE",FACE,{"disambiguationData":[OSD([subQ0])]})}),makeQuery(id+"F9.opExtrude","SWEPT_FACE",FACE,{"disambiguationData":[OSD([subQ0])]})]});}
            fillet(context, id + "F12", {"entities" : qUnion([Q0, Q1, Q2, Q3]), "radius" : .2 * mm, "tangentPropagation" : true, "allowEdgeOverflow" : false});
        }
        {
            var Q0;
            {var subQ0=sQuery(id+"F7.wireOp",EDGE,"E5.sketch_text.stroke-112");Q0=makeQuery(id+"F9.boolean.opBoolean","MERGE",FACE,{"derivedFrom":[makeQuery(id+"F8.boolean.opBoolean","COPY",FACE,{"derivedFrom":makeQuery(id+"F8.opExtrude","SWEPT_FACE",FACE,{"disambiguationData":[OSD([subQ0])]})}),makeQuery(id+"F9.opExtrude","SWEPT_FACE",FACE,{"disambiguationData":[OSD([subQ0])]})]});}
            var Q1;
            {var subQ0=sQuery(id+"F7.wireOp",EDGE,"E5.sketch_text.stroke-113");Q1=makeQuery(id+"F9.boolean.opBoolean","MERGE",FACE,{"derivedFrom":[makeQuery(id+"F8.boolean.opBoolean","COPY",FACE,{"derivedFrom":makeQuery(id+"F8.opExtrude","SWEPT_FACE",FACE,{"disambiguationData":[OSD([subQ0])]})}),makeQuery(id+"F9.opExtrude","SWEPT_FACE",FACE,{"disambiguationData":[OSD([subQ0])]})]});}
            var Q2;
            {var subQ0=sQuery(id+"F7.wireOp",EDGE,"E5.sketch_text.stroke-114");Q2=makeQuery(id+"F9.boolean.opBoolean","MERGE",FACE,{"derivedFrom":[makeQuery(id+"F8.boolean.opBoolean","COPY",FACE,{"derivedFrom":makeQuery(id+"F8.opExtrude","SWEPT_FACE",FACE,{"disambiguationData":[OSD([subQ0])]})}),makeQuery(id+"F9.opExtrude","SWEPT_FACE",FACE,{"disambiguationData":[OSD([subQ0])]})]});}
            var Q3;
            Q3=makeQuery(id+"F9.boolean.opBoolean","COPY",EDGE,{"derivedFrom":makeQuery(id+"F9.opExtrude","CAP_EDGE",EDGE,{"disambiguationData":[OSD([sQuery(id+"F7.wireOp",EDGE,"E5.sketch_text.stroke-115")])],"isStart":false})});
            var Q4;
            {var subQ0=sQuery(id+"F7.wireOp",EDGE,"E5.sketch_text.stroke-115");Q4=makeQuery(id+"F9.boolean.opBoolean","MERGE",FACE,{"derivedFrom":[makeQuery(id+"F8.boolean.opBoolean","COPY",FACE,{"derivedFrom":makeQuery(id+"F8.opExtrude","SWEPT_FACE",FACE,{"disambiguationData":[OSD([subQ0])]})}),makeQuery(id+"F9.opExtrude","SWEPT_FACE",FACE,{"disambiguationData":[OSD([subQ0])]})]});}
            var Q5;
            {var subQ0=sQuery(id+"F7.wireOp",EDGE,"E5.sketch_text.stroke-116");Q5=makeQuery(id+"F9.boolean.opBoolean","MERGE",FACE,{"derivedFrom":[makeQuery(id+"F8.boolean.opBoolean","COPY",FACE,{"derivedFrom":makeQuery(id+"F8.opExtrude","SWEPT_FACE",FACE,{"disambiguationData":[OSD([subQ0])]})}),makeQuery(id+"F9.opExtrude","SWEPT_FACE",FACE,{"disambiguationData":[OSD([subQ0])]})]});}
            var Q6;
            {var subQ0=sQuery(id+"F7.wireOp",EDGE,"E5.sketch_text.stroke-117");Q6=makeQuery(id+"F9.boolean.opBoolean","MERGE",FACE,{"derivedFrom":[makeQuery(id+"F8.boolean.opBoolean","COPY",FACE,{"derivedFrom":makeQuery(id+"F8.opExtrude","SWEPT_FACE",FACE,{"disambiguationData":[OSD([subQ0])]})}),makeQuery(id+"F9.opExtrude","SWEPT_FACE",FACE,{"disambiguationData":[OSD([subQ0])]})]});}
            var Q7;
            {var subQ0=sQuery(id+"F7.wireOp",EDGE,"E5.sketch_text.stroke-118");Q7=makeQuery(id+"F9.boolean.opBoolean","MERGE",FACE,{"derivedFrom":[makeQuery(id+"F8.boolean.opBoolean","COPY",FACE,{"derivedFrom":makeQuery(id+"F8.opExtrude","SWEPT_FACE",FACE,{"disambiguationData":[OSD([subQ0])]})}),makeQuery(id+"F9.opExtrude","SWEPT_FACE",FACE,{"disambiguationData":[OSD([subQ0])]})]});}
            var Q8;
            {var subQ0=sQuery(id+"F7.wireOp",EDGE,"E5.sketch_text.stroke-119");Q8=makeQuery(id+"F9.boolean.opBoolean","MERGE",FACE,{"derivedFrom":[makeQuery(id+"F8.boolean.opBoolean","COPY",FACE,{"derivedFrom":makeQuery(id+"F8.opExtrude","SWEPT_FACE",FACE,{"disambiguationData":[OSD([subQ0])]})}),makeQuery(id+"F9.opExtrude","SWEPT_FACE",FACE,{"disambiguationData":[OSD([subQ0])]})]});}
            var Q9;
            Q9=makeQuery(id+"F8.boolean.opBoolean","INTERSECT",EDGE,{"derivedFrom":[makeQuery(id+"F1.opExtrude","SWEPT_FACE",FACE,{"disambiguationData":[OSD([sQuery(id+"F0.wireOp",EDGE,"E0")])]}),makeQuery(id+"F8.opExtrude","SWEPT_FACE",FACE,{"disambiguationData":[OSD([sQuery(id+"F7.wireOp",EDGE,"E5.sketch_text.stroke-102")])]})]});
            var Q10;
            Q10=makeQuery(id+"F9.boolean.opBoolean","COPY",EDGE,{"derivedFrom":makeQuery(id+"F9.opExtrude","CAP_EDGE",EDGE,{"disambiguationData":[OSD([sQuery(id+"F7.wireOp",EDGE,"E5.sketch_text.stroke-102")])],"isStart":false})});
            fillet(context, id + "F13", {"entities" : qUnion([Q0, Q1, Q2, Q3, Q4, Q5, Q6, Q7, Q8, Q9, Q10]), "radius" : .2 * mm, "tangentPropagation" : true, "allowEdgeOverflow" : false});
        }
        {
            var Q0;
            {var subQ0=sQuery(id+"F7.wireOp",EDGE,"E5.sketch_text.stroke-125");Q0=makeQuery(id+"F9.boolean.opBoolean","MERGE",FACE,{"derivedFrom":[makeQuery(id+"F8.boolean.opBoolean","COPY",FACE,{"derivedFrom":makeQuery(id+"F8.opExtrude","SWEPT_FACE",FACE,{"disambiguationData":[OSD([subQ0])]})}),makeQuery(id+"F9.opExtrude","SWEPT_FACE",FACE,{"disambiguationData":[OSD([subQ0])]})]});}
            var Q1;
            {var subQ0=sQuery(id+"F7.wireOp",EDGE,"E5.sketch_text.stroke-141");Q1=makeQuery(id+"F9.boolean.opBoolean","MERGE",FACE,{"derivedFrom":[makeQuery(id+"F8.boolean.opBoolean","COPY",FACE,{"derivedFrom":makeQuery(id+"F8.opExtrude","SWEPT_FACE",FACE,{"disambiguationData":[OSD([subQ0])]})}),makeQuery(id+"F9.opExtrude","SWEPT_FACE",FACE,{"disambiguationData":[OSD([subQ0])]})]});}
            var Q2;
            {var subQ0=sQuery(id+"F7.wireOp",EDGE,"E5.sketch_text.stroke-133");Q2=makeQuery(id+"F9.boolean.opBoolean","MERGE",FACE,{"derivedFrom":[makeQuery(id+"F8.boolean.opBoolean","COPY",FACE,{"derivedFrom":makeQuery(id+"F8.opExtrude","SWEPT_FACE",FACE,{"disambiguationData":[OSD([subQ0])]})}),makeQuery(id+"F9.opExtrude","SWEPT_FACE",FACE,{"disambiguationData":[OSD([subQ0])]})]});}
            fillet(context, id + "F14", {"entities" : qUnion([Q0, Q1, Q2]), "radius" : .2 * mm, "tangentPropagation" : true, "allowEdgeOverflow" : false});
        }
        {
            var Q0;
            Q0=qCreatedBy(makeId("Top.planeOp"),FACE);
            cPlane(context, id + "F15", {"entities" : qUnion([Q0]), "cplaneType" : CPlaneType.OFFSET, "offset" : 40 * mm, "width" : 150 * mm, "height" : 150 * mm});
        }
        {
            var Q0;
            Q0=qCreatedBy(makeId("Right.planeOp"),FACE);
            cPlane(context, id + "F16", {"entities" : qUnion([Q0]), "cplaneType" : CPlaneType.OFFSET, "offset" : 20 * mm, "width" : 150 * mm, "height" : 150 * mm});
        }
        {
            var Q0;
            Q0=qCreatedBy(id+"F16.planeOp",FACE);
            var sketch = newSketch(context, id + "F17", { "sketchPlane" : qUnion([Q0])});
            skCircle(sketch, "E6", {"center": v(0, 11.39) * mm, "radius": 3.5 * mm});
            skCircle(sketch, "E7", {"center": v(0, 67.46) * mm, "radius": 3.5 * mm});
            skSolve(sketch);
        }
        {
            var Q0;
            Q0=qCreatedBy(makeId("Front.planeOp"),FACE);
            var sketch = newSketch(context, id + "F18", { "sketchPlane" : qUnion([Q0])});
            skLineSegment(sketch, "E8.0", {"start": v(20, 70.96) * mm, "end": v(20, 63.96) * mm});
            skPoint(sketch, "E9.0", {"position": v(20, 67.46) * mm});
            skPoint(sketch, "E10.0", {"position": v(20, 11.39) * mm});
            skLineSegment(sketch, "E11", {"start": v(20, 67.46) * mm, "end": v(31.17, 59.3) * mm});
            skLineSegment(sketch, "E12", {"start": v(31.17, 59.3) * mm, "end": v(31.17, 11.39) * mm});
            skLineSegment(sketch, "E13", {"start": v(31.17, 11.39) * mm, "end": v(20, 11.39) * mm});
            skLineSegment(sketch, "E14", {"start": v(31.17, 11.39) * mm, "end": v(31.17, -6.53) * mm});
            skSolve(sketch);
        }
        {
            var Q0;
            Q0=makeQuery(id+"F17.imprint","IMPRINT",FACE,{"disambiguationData":[TD([[makeQuery(id+"F17.imprint","IMPRINT",EDGE,{"derivedFrom":sQuery(id+"F17.wireOp",EDGE,"E6")}),1.0]])]});
            var Q1;
            Q1=makeQuery(id+"F17.imprint","IMPRINT",FACE,{"disambiguationData":[TD([[makeQuery(id+"F17.imprint","IMPRINT",EDGE,{"derivedFrom":sQuery(id+"F17.wireOp",EDGE,"E7")}),1.0]])]});
            extrude(context, id + "F19", {"entities" : qUnion([Q0, Q1]), "operationType" : NewBodyOperationType.ADD, "depth" : 1 * mm, "offsetDistance" : 25 * mm});
        }
        {
            var Q0;
            Q0=makeQuery(id+"F19.opExtrude","CAP_FACE",FACE,{"disambiguationData":[OSD([sQuery(id+"F17.wireOp",EDGE,"E7")])],"isStart":false});
            var Q1;
            Q1=sQuery(id+"F18.wireOp",EDGE,"E11");
            var Q2;
            Q2=sQuery(id+"F18.wireOp",EDGE,"E12");
            var Q3;
            Q3=sQuery(id+"F18.wireOp",EDGE,"E14");
            sweep(context, id + "F20", {"profiles" : qUnion([Q0]), "path" : qUnion([Q1, Q2, Q3])});
        }
        {
            var Q0;
            Q0=makeQuery(id+"F19.opExtrude","CAP_FACE",FACE,{"disambiguationData":[OSD([sQuery(id+"F17.wireOp",EDGE,"E6")])],"isStart":false});
            var Q1;
            Q1=sQuery(id+"F18.wireOp",EDGE,"E13");
            sweep(context, id + "F21", {"profiles" : qUnion([Q0]), "path" : qUnion([Q1])});
        }
        {
            var Q0;
            Q0=makeQuery(id+"F1.opExtrude","CAP_FACE",FACE,{"disambiguationData":[OSD([sQuery(id+"F0.wireOp",EDGE,"E0")])],"isStart":true});
            var sketch = newSketch(context, id + "F22", { "sketchPlane" : qUnion([Q0])});
            skCircle(sketch, "E15", {"center": v(0, 0) * mm, "radius": 18 * mm});
            skSolve(sketch);
        }
        {
            var Q0;
            Q0=makeQuery(id+"F22.imprint","IMPRINT",FACE,{"disambiguationData":[TD([[makeQuery(id+"F22.imprint","IMPRINT",EDGE,{"derivedFrom":sQuery(id+"F22.wireOp",EDGE,"E15")}),1.0]])]});
            extrude(context, id + "F23", {"entities" : qUnion([Q0]), "operationType" : NewBodyOperationType.REMOVE, "oppositeDirection" : true, "depth" : 5.2 * mm, "offsetDistance" : 25 * mm});
        }
        {
            var Q0;
            Q0=makeQuery(id+"F19.opExtrude","CAP_FACE",FACE,{"disambiguationData":[OSD([sQuery(id+"F17.wireOp",EDGE,"E6")])],"isStart":false});
            var sketch = newSketch(context, id + "F24", { "sketchPlane" : qUnion([Q0])});
            skCircle(sketch, "E16", {"center": v(0, 11.39) * mm, "radius": 3.59 * mm});
            skSolve(sketch);
        }
        {
            var Q0;
            Q0 = qSketchRegion(id + "F24", true);
            extrude(context, id + "F25", {"entities" : qUnion([Q0]), "endBound" : BoundingType.SYMMETRIC, "depth" : 7 * mm, "offsetDistance" : 25 * mm});
        }
        {
            var Q0;
            Q0=makeQuery(id+"F19.opExtrude","CAP_FACE",FACE,{"disambiguationData":[OSD([sQuery(id+"F17.wireOp",EDGE,"E7")])],"isStart":false});
            var sketch = newSketch(context, id + "F26", { "sketchPlane" : qUnion([Q0])});
            skPoint(sketch, "E17.0", {"position": v(0, 67.46) * mm});
            skCircle(sketch, "E18", {"center": v(0, 67.46) * mm, "radius": 3.41 * mm});
            skSolve(sketch);
        }
        {
            var Q0;
            Q0 = qSketchRegion(id + "F26", true);
            extrude(context, id + "F27", {"entities" : qUnion([Q0]), "endBound" : BoundingType.SYMMETRIC, "depth" : 1 * mm, "offsetDistance" : 25 * mm});
        }
    });
